# Revit family: VL2xGL200xWS840xxB
name_source: partatom
category: Leuchten
units: mm (PartAtom-declared; Revit-internal decimal feet)

## family parameters
Basisbauteil = Fläche
Beim Laden mit Abzugskörper schneiden = Nein
Bemaßung runder Anschluss = Durchmesser verwenden
Gemeinsam genutzt = Nein
Lichtquelle = Ja
OmniClass-Nummer = 23.80.70.11
OmniClass-Titel = Luminaries for Internal Lighting
Raumberechnungspunkt = Nein
Teiletyp = Normal

## types (12) — shared parameters
Baugruppenkennzeichen = D5020200
Datei für fotometrisches Netz = Master_VLxx-GLxxxB_IP20.IES
Emissionsform beim Rendern sichtbar = Nein
Farbfilter = 16777215
Farbtemperaturverschiebung bei Dämpfen der Lampe = <Keine Auswahl>
Hersteller = RIDI Leuchten GmbH
Lampe = LED
Neigungswinkel = 90.00°
URL = www.ridi.de
Von Breite des Rechtecks ausssenden = 1979 mm  [stored 6.49278 ft]
Von Länge des Rechtecks aussenden = 61 mm  [stored 0.200131 ft]
brand = RIDI
conformity mark = CE
electrical safety class = 1
height = 64 mm  [stored 0.209974 ft]
ingress protection (IP) code = IP20
length = 2000 mm  [stored 6.56168 ft]
nominal frequency = 50-60Hz
nominal voltage = 230
voltage type (AC, DC, UC) = AC
weight = 2,1kg
width = 67 mm
zero-valued in all types: Vorgabe-Ansicht

## per-type parameters (varying)
| type | Modell | Scheinlast | rated input power |
| VL2P-GL200-5FLWS840B2000 | 2550038 | 111 VA | 111 |
| VL2E-GL200-5FLWS840B1100 | 2550066 | 66 VA | 66 |
| VL2P-GL200-5FLWS840B1100 | 2550072 | 61 VA | 61 |
| VL2S-GL200-5FLWS840B1200 | 2550083 | 67 VA | 67 |
| VL2S-GL200-5FLWS840B1700 | 2550085 | 94 VA | 94 |
| VL2P-GL200-7DAWS840B2000 | 2560038 | 112 VA | 112 |
| VL2E-GL200-7DAWS840B1100 | 2560066 | 67 VA | 67 |
| VL2P-GL200-7DAWS840B1100 | 2560072 | 61 VA | 61 |
| VL2S-GL200-7DAWS840B1200 | 2560083 | 67 VA | 67 |
| VL2S-GL200-7DAWS840B1700 | 2560085 | 97 VA | 97 |
| VL2P-GL200-5NDWS840B0600 | 2550107 | 29 VA | 29 |
| VL2P-GL200-7DAWS840B0600 | 2560107 | 29 VA | 29 |

note: column(s) folded — value = type name in every type: product name

note: [stored X ft] marks values corroborated as IEEE doubles in the binary element streams (Revit-internal decimal feet)
